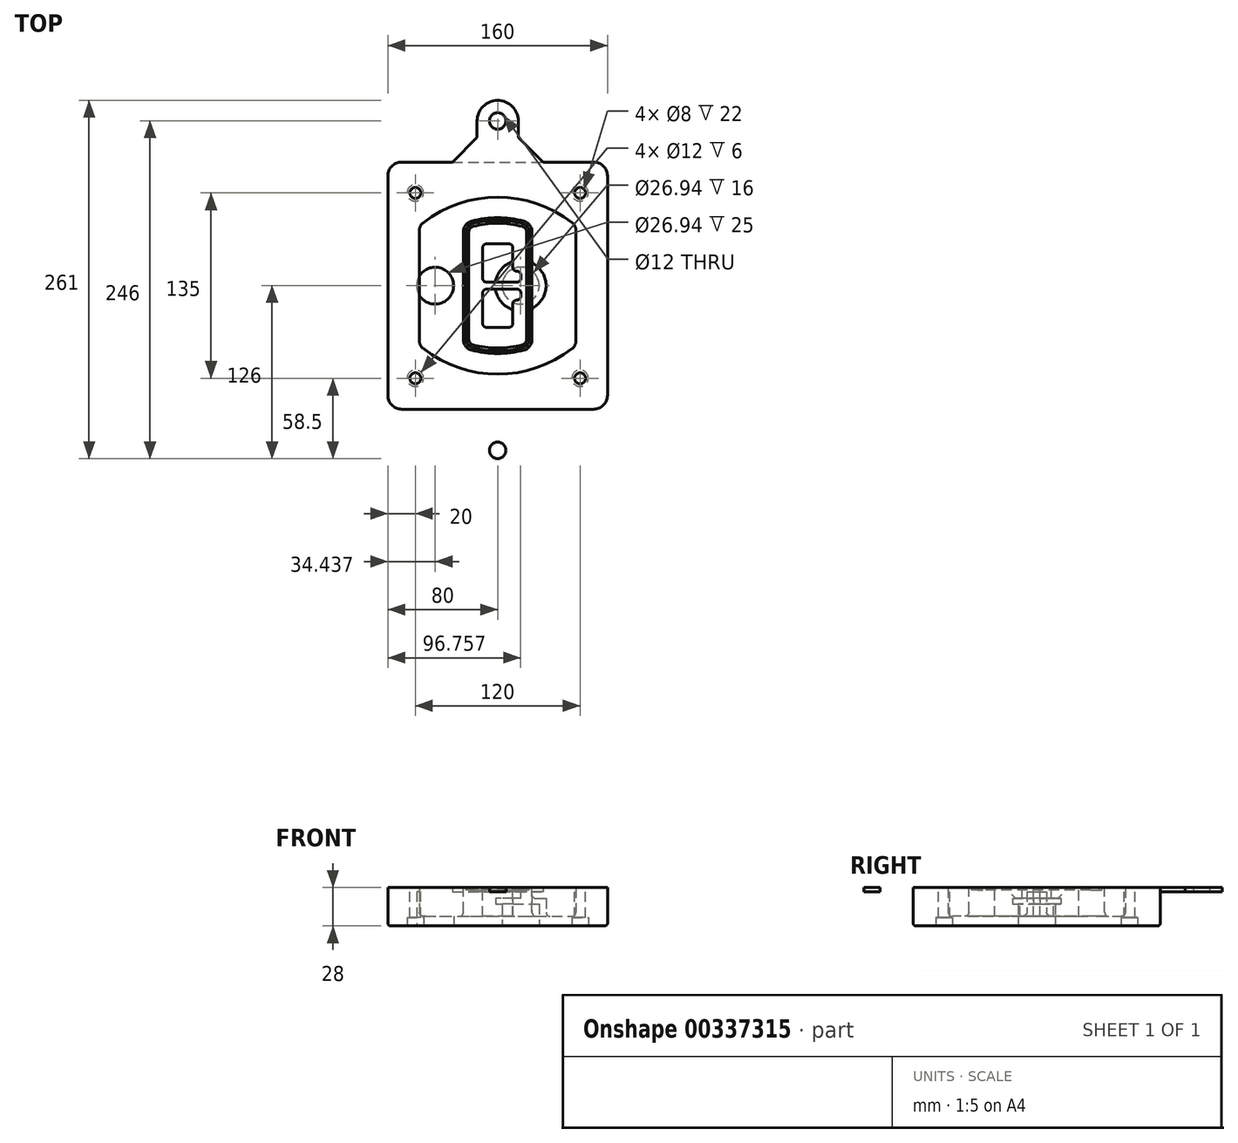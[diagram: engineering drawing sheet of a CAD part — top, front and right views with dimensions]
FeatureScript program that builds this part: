
annotation { "Feature Type Name" : "Feature", "Feature Type Description" : "" }
export const myFeature = defineFeature(function(context is Context, id is Id, definition is map)
    precondition{}
    {
        {
            var Q0;
            Q0=qCreatedBy(makeId("Top.planeOp"),FACE);
            var sketch = newSketch(context, id + "F0", { "sketchPlane" : qUnion([Q0])});
            skPoint(sketch, "E0.rect.middle", {"position": v(0, 0) * mm});
            skLineSegment(sketch, "E1.bottom", {"start": v(-70, -90) * mm, "end": v(70, -90) * mm});
            skLineSegment(sketch, "E1.top", {"start": v(-70, 90) * mm, "end": v(70, 90) * mm});
            skLineSegment(sketch, "E1.left", {"start": v(-80, -80) * mm, "end": v(-80, 80) * mm});
            skLineSegment(sketch, "E1.right", {"start": v(80, -80) * mm, "end": v(80, 80) * mm});
            skLineSegment(sketch, "E2", {"start": v(-80, 90) * mm, "end": v(80, -90) * mm, "construction": true});
            skLineSegment(sketch, "E3", {"start": v(80, 90) * mm, "end": v(-80, -90) * mm, "construction": true});
            skCircle(sketch, "E4", {"center": v(-60, 67.5) * mm, "radius": 4 * mm});
            skCircle(sketch, "E5", {"center": v(60, 67.5) * mm, "radius": 4 * mm});
            skCircle(sketch, "E6", {"center": v(60, -67.5) * mm, "radius": 4 * mm});
            skCircle(sketch, "E7", {"center": v(-60, -67.5) * mm, "radius": 4 * mm});
            skLineSegment(sketch, "E8", {"start": v(-60, 67.5) * mm, "end": v(60, 67.5) * mm, "construction": true});
            skLineSegment(sketch, "E9", {"start": v(60, 67.5) * mm, "end": v(60, -67.5) * mm, "construction": true});
            skLineSegment(sketch, "E10", {"start": v(60, -67.5) * mm, "end": v(-60, -67.5) * mm, "construction": true});
            skLineSegment(sketch, "E11", {"start": v(-60, -67.5) * mm, "end": v(-60, 67.5) * mm, "construction": true});
            skLineSegment(sketch, "E12", {"start": v(-60, 40.3) * mm, "end": v(-60, -40.3) * mm});
            skLineSegment(sketch, "E13", {"start": v(60, 40.3) * mm, "end": v(60, -40.3) * mm});
            skArc(sketch, "E14", {"start": v(56.15, 48.18) * mm, "mid": v(0, 67.5) * mm, "end": v(-56.15, 48.18) * mm});
            skArc(sketch, "E15", {"start": v(-56.15, -48.18) * mm, "mid": v(0, -67.5) * mm, "end": v(56.15, -48.18) * mm});
            skLineSegment(sketch, "E16", {"start": v(-60, 0) * mm, "end": v(60, 0) * mm, "construction": true});
            skPoint(sketch, "E17.visualSharp", {"position": v(-60, -45) * mm});
            skArc(sketch, "E17.filletArc", {"start": v(-60, -40.3) * mm, "mid": v(-58.99, -44.68) * mm, "end": v(-56.15, -48.18) * mm});
            skPoint(sketch, "E18.visualSharp", {"position": v(-60, 45) * mm});
            skArc(sketch, "E18.filletArc", {"start": v(-56.15, 48.18) * mm, "mid": v(-58.99, 44.68) * mm, "end": v(-60, 40.3) * mm});
            skPoint(sketch, "E19.visualSharp", {"position": v(60, 45) * mm});
            skArc(sketch, "E19.filletArc", {"start": v(60, 40.3) * mm, "mid": v(58.99, 44.68) * mm, "end": v(56.15, 48.18) * mm});
            skPoint(sketch, "E20.visualSharp", {"position": v(60, -45) * mm});
            skArc(sketch, "E20.filletArc", {"start": v(56.15, -48.18) * mm, "mid": v(58.99, -44.68) * mm, "end": v(60, -40.3) * mm});
            skPoint(sketch, "E21.visualSharp", {"position": v(-80, 90) * mm});
            skArc(sketch, "E21.filletArc", {"start": v(-70, 90) * mm, "mid": v(-77.07, 87.07) * mm, "end": v(-80, 80) * mm});
            skPoint(sketch, "E22.visualSharp", {"position": v(80, 90) * mm});
            skArc(sketch, "E22.filletArc", {"start": v(80, 80) * mm, "mid": v(77.07, 87.07) * mm, "end": v(70, 90) * mm});
            skPoint(sketch, "E23.visualSharp", {"position": v(80, -90) * mm});
            skArc(sketch, "E23.filletArc", {"start": v(70, -90) * mm, "mid": v(77.07, -87.07) * mm, "end": v(80, -80) * mm});
            skPoint(sketch, "E24.visualSharp", {"position": v(-80, -90) * mm});
            skArc(sketch, "E24.filletArc", {"start": v(-80, -80) * mm, "mid": v(-77.07, -87.07) * mm, "end": v(-70, -90) * mm});
            skArc(sketch, "E25.0", {"start": v(57, 40.3) * mm, "mid": v(56.3, 43.36) * mm, "end": v(54.3, 45.81) * mm});
            skLineSegment(sketch, "E25.1", {"start": v(57, 40.3) * mm, "end": v(57, -40.3) * mm});
            skArc(sketch, "E25.2", {"start": v(54.3, -45.81) * mm, "mid": v(56.3, -43.36) * mm, "end": v(57, -40.3) * mm});
            skArc(sketch, "E25.3", {"start": v(-54.3, -45.81) * mm, "mid": v(0, -64.5) * mm, "end": v(54.3, -45.81) * mm});
            skArc(sketch, "E25.4", {"start": v(-57, -40.3) * mm, "mid": v(-56.3, -43.36) * mm, "end": v(-54.3, -45.81) * mm});
            skArc(sketch, "E25.5", {"start": v(54.3, 45.81) * mm, "mid": v(0, 64.5) * mm, "end": v(-54.3, 45.81) * mm});
            skLineSegment(sketch, "E25.6", {"start": v(-57, 40.3) * mm, "end": v(-57, -40.3) * mm});
            skArc(sketch, "E25.7", {"start": v(-54.3, 45.81) * mm, "mid": v(-56.3, 43.36) * mm, "end": v(-57, 40.3) * mm});
            skArc(sketch, "E26.0", {"start": v(-58.62, 51.33) * mm, "mid": v(-62.58, 46.43) * mm, "end": v(-64, 40.3) * mm});
            skArc(sketch, "E26.1", {"start": v(58.62, 51.33) * mm, "mid": v(0, 71.5) * mm, "end": v(-58.62, 51.33) * mm});
            skArc(sketch, "E26.2", {"start": v(64, 40.3) * mm, "mid": v(62.58, 46.43) * mm, "end": v(58.62, 51.33) * mm});
            skLineSegment(sketch, "E26.3", {"start": v(64, 40.3) * mm, "end": v(64, -40.3) * mm});
            skArc(sketch, "E26.4", {"start": v(58.62, -51.33) * mm, "mid": v(62.58, -46.43) * mm, "end": v(64, -40.3) * mm});
            skLineSegment(sketch, "E26.5", {"start": v(-64, 40.3) * mm, "end": v(-64, -40.3) * mm});
            skArc(sketch, "E26.6", {"start": v(-58.62, -51.33) * mm, "mid": v(0, -71.5) * mm, "end": v(58.62, -51.33) * mm});
            skArc(sketch, "E26.7", {"start": v(-64, -40.3) * mm, "mid": v(-62.58, -46.43) * mm, "end": v(-58.62, -51.33) * mm});
            skSolve(sketch);
        }
        {
            var Q0;
            Q0=makeQuery(id+"F0.imprint","IMPRINT",FACE,{"disambiguationData":[TD([[makeQuery(id+"F0.imprint","IMPRINT",EDGE,{"derivedFrom":sQuery(id+"F0.wireOp",EDGE,"E1.bottom")}),1.0]])]});
            var Q1;
            Q1=makeQuery(id+"F0.imprint","IMPRINT",FACE,{"disambiguationData":[TD([[makeQuery(id+"F0.imprint","IMPRINT",EDGE,{"derivedFrom":sQuery(id+"F0.wireOp",EDGE,"E12")}),1.0]])]});
            var Q2;
            Q2=makeQuery(id+"F0.imprint","IMPRINT",FACE,{"disambiguationData":[TD([[makeQuery(id+"F0.imprint","IMPRINT",EDGE,{"derivedFrom":sQuery(id+"F0.wireOp",EDGE,"E25.0")}),1.0]])]});
            var Q3;
            Q3=makeQuery(id+"F0.imprint","IMPRINT",FACE,{"disambiguationData":[TD([[makeQuery(id+"F0.imprint","IMPRINT",EDGE,{"derivedFrom":sQuery(id+"F0.wireOp",EDGE,"E12")}),-1.0]])]});
            extrude(context, id + "F1", {"entities" : qUnion([Q0, Q1, Q2, Q3]), "oppositeDirection" : true, "depth" : 25 * mm});
        }
        {
            var Q0;
            Q0=makeQuery(id+"F0.imprint","IMPRINT",FACE,{"disambiguationData":[TD([[makeQuery(id+"F0.imprint","IMPRINT",EDGE,{"derivedFrom":sQuery(id+"F0.wireOp",EDGE,"E12")}),1.0]])]});
            extrude(context, id + "F2", {"entities" : qUnion([Q0]), "operationType" : NewBodyOperationType.ADD, "depth" : 3 * mm});
        }
        {
            var Q0;
            Q0=makeQuery(id+"F0.imprint","IMPRINT",FACE,{"disambiguationData":[TD([[makeQuery(id+"F0.imprint","IMPRINT",EDGE,{"derivedFrom":sQuery(id+"F0.wireOp",EDGE,"E25.0")}),1.0]])]});
            extrude(context, id + "F3", {"entities" : qUnion([Q0]), "operationType" : NewBodyOperationType.REMOVE, "oppositeDirection" : true, "depth" : 18 * mm});
        }
        {
            var Q0;
            Q0=makeQuery(id+"F2.opExtrude","CAP_FACE",FACE,{"disambiguationData":[OSD([sQuery(id+"F0.wireOp",EDGE,"E12"),sQuery(id+"F0.wireOp",EDGE,"E13"),sQuery(id+"F0.wireOp",EDGE,"E14"),sQuery(id+"F0.wireOp",EDGE,"E15"),sQuery(id+"F0.wireOp",EDGE,"E17.filletArc"),sQuery(id+"F0.wireOp",EDGE,"E18.filletArc"),sQuery(id+"F0.wireOp",EDGE,"E19.filletArc"),sQuery(id+"F0.wireOp",EDGE,"E20.filletArc"),sQuery(id+"F0.wireOp",EDGE,"E25.0"),sQuery(id+"F0.wireOp",EDGE,"E25.1"),sQuery(id+"F0.wireOp",EDGE,"E25.2"),sQuery(id+"F0.wireOp",EDGE,"E25.3"),sQuery(id+"F0.wireOp",EDGE,"E25.4"),sQuery(id+"F0.wireOp",EDGE,"E25.5"),sQuery(id+"F0.wireOp",EDGE,"E25.6"),sQuery(id+"F0.wireOp",EDGE,"E25.7")])],"isStart":false});
            var sketch = newSketch(context, id + "F4", { "sketchPlane" : qUnion([Q0])});
            skArc(sketch, "E27.0", {"start": v(-19.08, -46.97) * mm, "mid": v(0, -49.5) * mm, "end": v(19.08, -46.97) * mm});
            skArc(sketch, "E28.0", {"start": v(19.08, 46.97) * mm, "mid": v(0, 49.5) * mm, "end": v(-19.08, 46.97) * mm});
            skLineSegment(sketch, "E29", {"start": v(-25, 39.25) * mm, "end": v(-25, -39.25) * mm});
            skLineSegment(sketch, "E30", {"start": v(25, 39.25) * mm, "end": v(25, -39.25) * mm});
            skLineSegment(sketch, "E31", {"start": v(-25, 45.1) * mm, "end": v(25, 45.1) * mm, "construction": true});
            skLineSegment(sketch, "E32", {"start": v(-25, -45.1) * mm, "end": v(25, -45.1) * mm, "construction": true});
            skPoint(sketch, "E33.visualSharp", {"position": v(-25, 45.1) * mm});
            skArc(sketch, "E33.filletArc", {"start": v(-19.08, 46.97) * mm, "mid": v(-23.35, 44.11) * mm, "end": v(-25, 39.25) * mm});
            skPoint(sketch, "E34.visualSharp", {"position": v(25, 45.1) * mm});
            skArc(sketch, "E34.filletArc", {"start": v(25, 39.25) * mm, "mid": v(23.35, 44.11) * mm, "end": v(19.08, 46.97) * mm});
            skPoint(sketch, "E35.visualSharp", {"position": v(25, -45.1) * mm});
            skArc(sketch, "E35.filletArc", {"start": v(19.08, -46.97) * mm, "mid": v(23.35, -44.11) * mm, "end": v(25, -39.25) * mm});
            skPoint(sketch, "E36.visualSharp", {"position": v(-25, -45.1) * mm});
            skArc(sketch, "E36.filletArc", {"start": v(-25, -39.25) * mm, "mid": v(-23.35, -44.11) * mm, "end": v(-19.08, -46.97) * mm});
            skArc(sketch, "E37.0", {"start": v(54.3, 45.81) * mm, "mid": v(0, 64.5) * mm, "end": v(-54.3, 45.81) * mm});
            skArc(sketch, "E37.1", {"start": v(-54.3, 45.81) * mm, "mid": v(-56.3, 43.36) * mm, "end": v(-57, 40.3) * mm});
            skLineSegment(sketch, "E37.2", {"start": v(-57, 40.3) * mm, "end": v(-57, -40.3) * mm});
            skArc(sketch, "E37.3", {"start": v(-57, -40.3) * mm, "mid": v(-56.3, -43.36) * mm, "end": v(-54.3, -45.81) * mm});
            skArc(sketch, "E37.4", {"start": v(-54.3, -45.81) * mm, "mid": v(0, -64.5) * mm, "end": v(54.3, -45.81) * mm});
            skArc(sketch, "E37.5", {"start": v(54.3, -45.81) * mm, "mid": v(56.3, -43.36) * mm, "end": v(57, -40.3) * mm});
            skLineSegment(sketch, "E37.6", {"start": v(57, 40.3) * mm, "end": v(57, -40.3) * mm});
            skArc(sketch, "E37.7", {"start": v(57, 40.3) * mm, "mid": v(56.3, 43.36) * mm, "end": v(54.3, 45.81) * mm});
            skLineSegment(sketch, "E38.0", {"start": v(23, 39.25) * mm, "end": v(23, -39.25) * mm});
            skArc(sketch, "E38.1", {"start": v(18.56, -45.04) * mm, "mid": v(21.76, -42.9) * mm, "end": v(23, -39.25) * mm});
            skArc(sketch, "E38.2", {"start": v(-18.56, -45.04) * mm, "mid": v(0, -47.5) * mm, "end": v(18.56, -45.04) * mm});
            skArc(sketch, "E38.3", {"start": v(-23, -39.25) * mm, "mid": v(-21.76, -42.9) * mm, "end": v(-18.56, -45.04) * mm});
            skLineSegment(sketch, "E38.4", {"start": v(-23, 39.25) * mm, "end": v(-23, -39.25) * mm});
            skArc(sketch, "E38.5", {"start": v(23, 39.25) * mm, "mid": v(21.76, 42.9) * mm, "end": v(18.56, 45.04) * mm});
            skArc(sketch, "E38.6", {"start": v(-18.56, 45.04) * mm, "mid": v(-21.76, 42.9) * mm, "end": v(-23, 39.25) * mm});
            skArc(sketch, "E38.7", {"start": v(18.56, 45.04) * mm, "mid": v(0, 47.5) * mm, "end": v(-18.56, 45.04) * mm});
            skArc(sketch, "E39.0", {"start": v(21, 39.25) * mm, "mid": v(20.18, 41.68) * mm, "end": v(18.04, 43.1) * mm});
            skLineSegment(sketch, "E39.1", {"start": v(21, 39.25) * mm, "end": v(21, -39.25) * mm});
            skArc(sketch, "E39.2", {"start": v(18.04, -43.1) * mm, "mid": v(20.18, -41.68) * mm, "end": v(21, -39.25) * mm});
            skArc(sketch, "E39.3", {"start": v(-18.04, -43.1) * mm, "mid": v(0, -45.5) * mm, "end": v(18.04, -43.1) * mm});
            skArc(sketch, "E39.4", {"start": v(-21, -39.25) * mm, "mid": v(-20.18, -41.68) * mm, "end": v(-18.04, -43.1) * mm});
            skArc(sketch, "E39.5", {"start": v(18.04, 43.1) * mm, "mid": v(0, 45.5) * mm, "end": v(-18.04, 43.1) * mm});
            skLineSegment(sketch, "E39.6", {"start": v(-21, 39.25) * mm, "end": v(-21, -39.25) * mm});
            skArc(sketch, "E39.7", {"start": v(-18.04, 43.1) * mm, "mid": v(-20.18, 41.68) * mm, "end": v(-21, 39.25) * mm});
            skLineSegment(sketch, "E40", {"start": v(-25, 0) * mm, "end": v(25, 0) * mm, "construction": true});
            skLineSegment(sketch, "E41", {"start": v(-11, 5.5) * mm, "end": v(-11, 27.5) * mm});
            skLineSegment(sketch, "E42", {"start": v(-8, 30.5) * mm, "end": v(8, 30.5) * mm});
            skLineSegment(sketch, "E43", {"start": v(11, 27.5) * mm, "end": v(11, 13.5) * mm});
            skLineSegment(sketch, "E44", {"start": v(14, 10.5) * mm, "end": v(14, 10.5) * mm});
            skLineSegment(sketch, "E45", {"start": v(17, 7.5) * mm, "end": v(17, 5.5) * mm});
            skLineSegment(sketch, "E46", {"start": v(14, 2.5) * mm, "end": v(-8, 2.5) * mm});
            skPoint(sketch, "E47.visualSharp", {"position": v(-11, 30.5) * mm});
            skArc(sketch, "E47.filletArc", {"start": v(-8, 30.5) * mm, "mid": v(-10.12, 29.62) * mm, "end": v(-11, 27.5) * mm});
            skPoint(sketch, "E48.visualSharp", {"position": v(11, 30.5) * mm});
            skArc(sketch, "E48.filletArc", {"start": v(11, 27.5) * mm, "mid": v(10.12, 29.62) * mm, "end": v(8, 30.5) * mm});
            skPoint(sketch, "E49.visualSharp", {"position": v(11, 10.5) * mm});
            skArc(sketch, "E49.filletArc", {"start": v(11, 13.5) * mm, "mid": v(11.88, 11.38) * mm, "end": v(14, 10.5) * mm});
            skPoint(sketch, "E50.visualSharp", {"position": v(17, 10.5) * mm});
            skArc(sketch, "E50.filletArc", {"start": v(17, 7.5) * mm, "mid": v(16.12, 9.62) * mm, "end": v(14, 10.5) * mm});
            skPoint(sketch, "E51.visualSharp", {"position": v(17, 2.5) * mm});
            skArc(sketch, "E51.filletArc", {"start": v(14, 2.5) * mm, "mid": v(16.12, 3.38) * mm, "end": v(17, 5.5) * mm});
            skPoint(sketch, "E52.visualSharp", {"position": v(-11, 2.5) * mm});
            skArc(sketch, "E52.filletArc", {"start": v(-11, 5.5) * mm, "mid": v(-10.12, 3.38) * mm, "end": v(-8, 2.5) * mm});
            skLineSegment(sketch, "E53.0.MirrorCS", {"start": v(14, -2.5) * mm, "end": v(-8, -2.5) * mm});
            skArc(sketch, "E54.0.MirrorCS", {"start": v(-11, -5.5) * mm, "mid": v(-10.12, -3.38) * mm, "end": v(-8, -2.5) * mm});
            skLineSegment(sketch, "E55.0.MirrorCS", {"start": v(-11, -5.5) * mm, "end": v(-11, -27.5) * mm});
            skArc(sketch, "E56.0.MirrorCS", {"start": v(-8, -30.5) * mm, "mid": v(-10.12, -29.62) * mm, "end": v(-11, -27.5) * mm});
            skLineSegment(sketch, "E57.0.MirrorCS", {"start": v(-8, -30.5) * mm, "end": v(8, -30.5) * mm});
            skArc(sketch, "E58.0.MirrorCS", {"start": v(11, -27.5) * mm, "mid": v(10.12, -29.62) * mm, "end": v(8, -30.5) * mm});
            skLineSegment(sketch, "E59.0.MirrorCS", {"start": v(11, -27.5) * mm, "end": v(11, -13.5) * mm});
            skArc(sketch, "E60.0.MirrorCS", {"start": v(11, -13.5) * mm, "mid": v(11.88, -11.38) * mm, "end": v(14, -10.5) * mm});
            skArc(sketch, "E61.0.MirrorCS", {"start": v(17, -7.5) * mm, "mid": v(16.12, -9.62) * mm, "end": v(14, -10.5) * mm});
            skLineSegment(sketch, "E62.0.MirrorCS", {"start": v(17, -7.5) * mm, "end": v(17, -5.5) * mm});
            skArc(sketch, "E63.0.MirrorCS", {"start": v(14, -2.5) * mm, "mid": v(16.12, -3.38) * mm, "end": v(17, -5.5) * mm});
            skSolve(sketch);
        }
        {
            var Q0;
            Q0=makeQuery(id+"F4.imprint","IMPRINT",FACE,{"disambiguationData":[TD([[makeQuery(id+"F4.imprint","IMPRINT",EDGE,{"derivedFrom":sQuery(id+"F4.wireOp",EDGE,"E27.0")}),1.0]])]});
            var Q1;
            Q1=makeQuery(id+"F4.imprint","IMPRINT",FACE,{"disambiguationData":[TD([[makeQuery(id+"F4.imprint","IMPRINT",EDGE,{"derivedFrom":sQuery(id+"F4.wireOp",EDGE,"E38.0")}),-1.0]])]});
            var Q2;
            Q2=makeQuery(id+"F4.imprint","IMPRINT",FACE,{"disambiguationData":[TD([[makeQuery(id+"F4.imprint","IMPRINT",EDGE,{"derivedFrom":sQuery(id+"F4.wireOp",EDGE,"E39.0")}),1.0]])]});
            extrude(context, id + "F5", {"entities" : qUnion([Q0, Q1, Q2]), "operationType" : NewBodyOperationType.ADD, "endBound" : BoundingType.UP_TO_NEXT, "oppositeDirection" : true, "depth" : 25 * mm});
        }
        {
            var Q0;
            Q0=makeQuery(id+"F4.imprint","IMPRINT",FACE,{"disambiguationData":[TD([[makeQuery(id+"F4.imprint","IMPRINT",EDGE,{"derivedFrom":sQuery(id+"F4.wireOp",EDGE,"E38.0")}),-1.0]])]});
            extrude(context, id + "F6", {"entities" : qUnion([Q0]), "operationType" : NewBodyOperationType.REMOVE, "oppositeDirection" : true, "depth" : 2 * mm});
        }
        {
            var Q0;
            Q0=makeQuery(id+"F1.opExtrude","CAP_FACE",FACE,{"disambiguationData":[OSD([sQuery(id+"F0.wireOp",EDGE,"E1.bottom"),sQuery(id+"F0.wireOp",EDGE,"E1.top"),sQuery(id+"F0.wireOp",EDGE,"E1.left"),sQuery(id+"F0.wireOp",EDGE,"E1.right"),sQuery(id+"F0.wireOp",EDGE,"E4"),sQuery(id+"F0.wireOp",EDGE,"E5"),sQuery(id+"F0.wireOp",EDGE,"E6"),sQuery(id+"F0.wireOp",EDGE,"E7"),sQuery(id+"F0.wireOp",EDGE,"E21.filletArc"),sQuery(id+"F0.wireOp",EDGE,"E22.filletArc"),sQuery(id+"F0.wireOp",EDGE,"E23.filletArc"),sQuery(id+"F0.wireOp",EDGE,"E24.filletArc")])],"isStart":false});
            var sketch = newSketch(context, id + "F7", { "sketchPlane" : qUnion([Q0])});
            skCircle(sketch, "E64", {"center": v(16.76, 0) * mm, "radius": 13.47 * mm});
            skCircle(sketch, "E65", {"center": v(-45.56, 0) * mm, "radius": 13.47 * mm});
            skLineSegment(sketch, "E66", {"start": v(80, 0) * mm, "end": v(-80, 0) * mm});
            skCircle(sketch, "E67", {"center": v(16.76, 0) * mm, "radius": 18.47 * mm});
            skCircle(sketch, "E68", {"center": v(60, -67.5) * mm, "radius": 6 * mm});
            skCircle(sketch, "E69", {"center": v(-60, -67.5) * mm, "radius": 6 * mm});
            skCircle(sketch, "E70", {"center": v(-60, 67.5) * mm, "radius": 6 * mm});
            skCircle(sketch, "E71", {"center": v(60, 67.5) * mm, "radius": 6 * mm});
            skSolve(sketch);
        }
        {
            var Q0;
            {var subQ1=sQuery(id+"F7.wireOp",EDGE,"E66");var subQ4=sQuery(id+"F7.wireOp",EDGE,"E64");var subQ6=makeQuery(id+"F7.imprint","INTERSECT",VERTEX,{"disambiguationData":[OD(0.0)],"derivedFrom":[subQ4,subQ1]});Q0=makeQuery(id+"F7.imprint","IMPRINT",FACE,{"disambiguationData":[TD([[makeQuery(id+"F7.imprint","IMPRINT",EDGE,{"disambiguationData":[TD([[subQ6,-1.0]])],"derivedFrom":subQ4}),-1.0]])]});}
            var Q1;
            {var subQ0=sQuery(id+"F7.wireOp",EDGE,"E66");var subQ1=sQuery(id+"F7.wireOp",EDGE,"E64");var subQ3=makeQuery(id+"F7.imprint","INTERSECT",VERTEX,{"disambiguationData":[OD(0.0)],"derivedFrom":[subQ1,subQ0]});Q1=makeQuery(id+"F7.imprint","IMPRINT",FACE,{"disambiguationData":[TD([[makeQuery(id+"F7.imprint","IMPRINT",EDGE,{"disambiguationData":[TD([[subQ3,-1.0]])],"derivedFrom":subQ1}),1.0]])]});}
            var Q2;
            {var subQ0=sQuery(id+"F7.wireOp",EDGE,"E66");var subQ1=sQuery(id+"F7.wireOp",EDGE,"E64");var subQ3=makeQuery(id+"F7.imprint","INTERSECT",VERTEX,{"disambiguationData":[OD(0.0)],"derivedFrom":[subQ1,subQ0]});Q2=makeQuery(id+"F7.imprint","IMPRINT",FACE,{"disambiguationData":[TD([[makeQuery(id+"F7.imprint","IMPRINT",EDGE,{"disambiguationData":[TD([[subQ3,1.0]])],"derivedFrom":subQ1}),1.0]])]});}
            var Q3;
            {var subQ1=sQuery(id+"F7.wireOp",EDGE,"E66");var subQ4=sQuery(id+"F7.wireOp",EDGE,"E64");var subQ6=makeQuery(id+"F7.imprint","INTERSECT",VERTEX,{"disambiguationData":[OD(0.0)],"derivedFrom":[subQ4,subQ1]});Q3=makeQuery(id+"F7.imprint","IMPRINT",FACE,{"disambiguationData":[TD([[makeQuery(id+"F7.imprint","IMPRINT",EDGE,{"disambiguationData":[TD([[subQ6,1.0]])],"derivedFrom":subQ4}),-1.0]])]});}
            extrude(context, id + "F8", {"entities" : qUnion([Q0, Q1, Q2, Q3]), "operationType" : NewBodyOperationType.ADD, "oppositeDirection" : true, "depth" : 20 * mm});
        }
        {
            var Q0;
            {var subQ0=sQuery(id+"F7.wireOp",EDGE,"E66");var subQ1=sQuery(id+"F7.wireOp",EDGE,"E64");var subQ3=makeQuery(id+"F7.imprint","INTERSECT",VERTEX,{"disambiguationData":[OD(0.0)],"derivedFrom":[subQ1,subQ0]});Q0=makeQuery(id+"F7.imprint","IMPRINT",FACE,{"disambiguationData":[TD([[makeQuery(id+"F7.imprint","IMPRINT",EDGE,{"disambiguationData":[TD([[subQ3,-1.0]])],"derivedFrom":subQ1}),1.0]])]});}
            var Q1;
            {var subQ0=sQuery(id+"F7.wireOp",EDGE,"E66");var subQ1=sQuery(id+"F7.wireOp",EDGE,"E64");var subQ3=makeQuery(id+"F7.imprint","INTERSECT",VERTEX,{"disambiguationData":[OD(0.0)],"derivedFrom":[subQ1,subQ0]});Q1=makeQuery(id+"F7.imprint","IMPRINT",FACE,{"disambiguationData":[TD([[makeQuery(id+"F7.imprint","IMPRINT",EDGE,{"disambiguationData":[TD([[subQ3,1.0]])],"derivedFrom":subQ1}),1.0]])]});}
            extrude(context, id + "F9", {"entities" : qUnion([Q0, Q1]), "operationType" : NewBodyOperationType.REMOVE, "oppositeDirection" : true, "depth" : 16 * mm});
        }
        {
            var Q0;
            {var subQ0=sQuery(id+"F7.wireOp",EDGE,"E66");var subQ1=sQuery(id+"F7.wireOp",EDGE,"E65");var subQ3=makeQuery(id+"F7.imprint","INTERSECT",VERTEX,{"disambiguationData":[OD(0.0)],"derivedFrom":[subQ1,subQ0]});Q0=makeQuery(id+"F7.imprint","IMPRINT",FACE,{"disambiguationData":[TD([[makeQuery(id+"F7.imprint","IMPRINT",EDGE,{"disambiguationData":[TD([[subQ3,-1.0]])],"derivedFrom":subQ1}),1.0]])]});}
            var Q1;
            {var subQ0=sQuery(id+"F7.wireOp",EDGE,"E66");var subQ1=sQuery(id+"F7.wireOp",EDGE,"E65");var subQ3=makeQuery(id+"F7.imprint","INTERSECT",VERTEX,{"disambiguationData":[OD(0.0)],"derivedFrom":[subQ1,subQ0]});Q1=makeQuery(id+"F7.imprint","IMPRINT",FACE,{"disambiguationData":[TD([[makeQuery(id+"F7.imprint","IMPRINT",EDGE,{"disambiguationData":[TD([[subQ3,1.0]])],"derivedFrom":subQ1}),1.0]])]});}
            extrude(context, id + "F10", {"entities" : qUnion([Q0, Q1]), "operationType" : NewBodyOperationType.REMOVE, "oppositeDirection" : true, "depth" : 25 * mm});
        }
        {
            var Q0;
            Q0=makeQuery(id+"F7.imprint","IMPRINT",FACE,{"disambiguationData":[TD([[makeQuery(id+"F7.imprint","IMPRINT",EDGE,{"derivedFrom":sQuery(id+"F7.wireOp",EDGE,"E68")}),1.0]])]});
            var Q1;
            Q1=makeQuery(id+"F7.imprint","IMPRINT",FACE,{"disambiguationData":[TD([[makeQuery(id+"F7.imprint","IMPRINT",EDGE,{"derivedFrom":makeQuery(id+"F1.opExtrude","CAP_EDGE",EDGE,{"disambiguationData":[OSD([sQuery(id+"F0.wireOp",EDGE,"E5")])],"isStart":false})}),-1.0]])]});
            var Q2;
            Q2=makeQuery(id+"F7.imprint","IMPRINT",FACE,{"disambiguationData":[TD([[makeQuery(id+"F7.imprint","IMPRINT",EDGE,{"derivedFrom":sQuery(id+"F7.wireOp",EDGE,"E69")}),1.0]])]});
            var Q3;
            Q3=makeQuery(id+"F7.imprint","IMPRINT",FACE,{"disambiguationData":[TD([[makeQuery(id+"F7.imprint","IMPRINT",EDGE,{"derivedFrom":makeQuery(id+"F1.opExtrude","CAP_EDGE",EDGE,{"disambiguationData":[OSD([sQuery(id+"F0.wireOp",EDGE,"E4")])],"isStart":false})}),-1.0]])]});
            var Q4;
            Q4=makeQuery(id+"F7.imprint","IMPRINT",FACE,{"disambiguationData":[TD([[makeQuery(id+"F7.imprint","IMPRINT",EDGE,{"derivedFrom":sQuery(id+"F7.wireOp",EDGE,"E70")}),1.0]])]});
            var Q5;
            Q5=makeQuery(id+"F7.imprint","IMPRINT",FACE,{"disambiguationData":[TD([[makeQuery(id+"F7.imprint","IMPRINT",EDGE,{"derivedFrom":makeQuery(id+"F1.opExtrude","CAP_EDGE",EDGE,{"disambiguationData":[OSD([sQuery(id+"F0.wireOp",EDGE,"E7")])],"isStart":false})}),-1.0]])]});
            var Q6;
            Q6=makeQuery(id+"F7.imprint","IMPRINT",FACE,{"disambiguationData":[TD([[makeQuery(id+"F7.imprint","IMPRINT",EDGE,{"derivedFrom":sQuery(id+"F7.wireOp",EDGE,"E71")}),1.0]])]});
            var Q7;
            Q7=makeQuery(id+"F7.imprint","IMPRINT",FACE,{"disambiguationData":[TD([[makeQuery(id+"F7.imprint","IMPRINT",EDGE,{"derivedFrom":makeQuery(id+"F1.opExtrude","CAP_EDGE",EDGE,{"disambiguationData":[OSD([sQuery(id+"F0.wireOp",EDGE,"E6")])],"isStart":false})}),-1.0]])]});
            extrude(context, id + "F11", {"entities" : qUnion([Q0, Q1, Q2, Q3, Q4, Q5, Q6, Q7]), "operationType" : NewBodyOperationType.REMOVE, "oppositeDirection" : true, "depth" : 6 * mm});
        }
        {
            var Q0;
            Q0=makeQuery(id+"F9.boolean.opBoolean","COPY",FACE,{"derivedFrom":makeQuery(id+"F9.opExtrude","CAP_FACE",FACE,{"disambiguationData":[OSD([sQuery(id+"F7.wireOp",EDGE,"E64")])],"isStart":false})});
            var sketch = newSketch(context, id + "F12", { "sketchPlane" : qUnion([Q0])});
            skArc(sketch, "E72.0", {"start": v(11, 17.55) * mm, "mid": v(2.57, 11.82) * mm, "end": v(-1.54, 2.5) * mm});
            skArc(sketch, "E72.1", {"start": v(-1.54, -2.5) * mm, "mid": v(2.57, -11.82) * mm, "end": v(11, -17.55) * mm});
            skLineSegment(sketch, "E73", {"start": v(-1.54, -2.5) * mm, "end": v(14, -2.5) * mm});
            skLineSegment(sketch, "E74.0", {"start": v(14, 2.5) * mm, "end": v(-1.54, 2.5) * mm});
            skArc(sketch, "E74.1", {"start": v(14, 2.5) * mm, "mid": v(16.12, 3.38) * mm, "end": v(17, 5.5) * mm});
            skLineSegment(sketch, "E74.2", {"start": v(17, 7.5) * mm, "end": v(17, 5.5) * mm});
            skArc(sketch, "E74.3", {"start": v(17, 7.5) * mm, "mid": v(16.12, 9.62) * mm, "end": v(14, 10.5) * mm});
            skArc(sketch, "E74.4", {"start": v(11, 13.5) * mm, "mid": v(11.88, 11.38) * mm, "end": v(14, 10.5) * mm});
            skLineSegment(sketch, "E74.5", {"start": v(11, 17.55) * mm, "end": v(11, 13.5) * mm});
            skLineSegment(sketch, "E74.7", {"start": v(14, -2.5) * mm, "end": v(-1.54, -2.5) * mm});
            skArc(sketch, "E74.8", {"start": v(14, -2.5) * mm, "mid": v(16.12, -3.38) * mm, "end": v(17, -5.5) * mm});
            skLineSegment(sketch, "E74.9", {"start": v(17, -7.5) * mm, "end": v(17, -5.5) * mm});
            skArc(sketch, "E74.10", {"start": v(17, -7.5) * mm, "mid": v(16.12, -9.62) * mm, "end": v(14, -10.5) * mm});
            skArc(sketch, "E74.11", {"start": v(11, -13.5) * mm, "mid": v(11.88, -11.38) * mm, "end": v(14, -10.5) * mm});
            skLineSegment(sketch, "E74.12", {"start": v(11, -17.55) * mm, "end": v(11, -13.5) * mm});
            skPoint(sketch, "E75.orphan", {"position": v(11, -27.5) * mm});
            skPoint(sketch, "E76.orphan", {"position": v(-8, -2.5) * mm});
            skPoint(sketch, "E77.orphan", {"position": v(-8, 2.5) * mm});
            skPoint(sketch, "E78.orphan", {"position": v(11, 27.5) * mm});
            skSolve(sketch);
        }
        {
            var Q0;
            {var subQ7=sQuery(id+"F12.wireOp",EDGE,"E72.0");var subQ14=sQuery(id+"F12.wireOp",EDGE,"E72.1");var subQ16=sQuery(id+"F12.wireOp",EDGE,"E74.1");var subQ18=sQuery(id+"F12.wireOp",EDGE,"E74.8");Q0=qUnion([makeQuery(id+"F12.imprint","IMPRINT",FACE,{"disambiguationData":[TD([[makeQuery(id+"F12.imprint","IMPRINT",EDGE,{"derivedFrom":subQ7}),1.0]])]}),makeQuery(id+"F12.imprint","IMPRINT",FACE,{"disambiguationData":[TD([[makeQuery(id+"F12.imprint","IMPRINT",EDGE,{"derivedFrom":subQ14}),1.0]])]}),makeQuery(id+"F12.imprint","IMPRINT",FACE,{"disambiguationData":[TD([[makeQuery(id+"F12.imprint","IMPRINT",EDGE,{"derivedFrom":subQ16}),1.0]])]}),makeQuery(id+"F12.imprint","IMPRINT",FACE,{"disambiguationData":[TD([[makeQuery(id+"F12.imprint","IMPRINT",EDGE,{"derivedFrom":subQ18}),-1.0]])]})]);}
            var Q1;
            Q1=makeQuery(id+"F5.boolean.opBoolean","SPLIT",FACE,{"disambiguationData":[TD([makeQuery(id+"F5.opExtrude","SWEPT_FACE",FACE,{"disambiguationData":[OSD([sQuery(id+"F4.wireOp",EDGE,"E41")])]})])],"derivedFrom":makeQuery(id+"F3.boolean.opBoolean","COPY",FACE,{"derivedFrom":makeQuery(id+"F3.opExtrude","CAP_FACE",FACE,{"disambiguationData":[OSD([sQuery(id+"F0.wireOp",EDGE,"E25.0"),sQuery(id+"F0.wireOp",EDGE,"E25.1"),sQuery(id+"F0.wireOp",EDGE,"E25.2"),sQuery(id+"F0.wireOp",EDGE,"E25.3"),sQuery(id+"F0.wireOp",EDGE,"E25.4"),sQuery(id+"F0.wireOp",EDGE,"E25.5"),sQuery(id+"F0.wireOp",EDGE,"E25.6"),sQuery(id+"F0.wireOp",EDGE,"E25.7")])],"isStart":false})})});
            extrude(context, id + "F13", {"entities" : qUnion([Q0]), "operationType" : NewBodyOperationType.REMOVE, "endBound" : BoundingType.UP_TO_SURFACE, "endBoundEntityFace" : qUnion([Q1]), "depth" : 25 * mm});
        }
        {
            var Q0;
            Q0=makeQuery(id+"F3.boolean.opBoolean","COPY",EDGE,{"derivedFrom":makeQuery(id+"F3.opExtrude","CAP_EDGE",EDGE,{"disambiguationData":[OSD([sQuery(id+"F0.wireOp",EDGE,"E25.6")])],"isStart":false})});
            var Q1;
            Q1=makeQuery(id+"F8.boolean.opBoolean","INTERSECT",EDGE,{"derivedFrom":[makeQuery(id+"F5.opExtrude","SWEPT_FACE",FACE,{"disambiguationData":[OSD([sQuery(id+"F4.wireOp",EDGE,"E30")])]}),makeQuery(id+"F8.opExtrude","CAP_FACE",FACE,{"disambiguationData":[OSD([sQuery(id+"F7.wireOp",EDGE,"E67")])],"isStart":false})]});
            var Q2;
            Q2=makeQuery(id+"F8.boolean.opBoolean","INTERSECT",EDGE,{"disambiguationData":[OD(1.0)],"derivedFrom":[makeQuery(id+"F5.opExtrude","SWEPT_FACE",FACE,{"disambiguationData":[OSD([sQuery(id+"F4.wireOp",EDGE,"E30")])]}),makeQuery(id+"F8.opExtrude","SWEPT_FACE",FACE,{"disambiguationData":[OSD([sQuery(id+"F7.wireOp",EDGE,"E67")])]})]});
            var Q3;
            {var subQ0=sQuery(id+"F4.wireOp",EDGE,"E30");Q3=makeQuery(id+"F8.boolean.opBoolean","SPLIT",EDGE,{"disambiguationData":[TD([makeQuery(id+"F5.opExtrude","SWEPT_FACE",FACE,{"disambiguationData":[OSD([sQuery(id+"F4.wireOp",EDGE,"E35.filletArc")])]})])],"derivedFrom":makeQuery(id+"F5.opExtrude","CAP_EDGE",EDGE,{"disambiguationData":[OSD([subQ0])],"isStart":false})});}
            var Q4;
            {var subQ0=sQuery(id+"F0.wireOp",EDGE,"E25.7");var subQ1=sQuery(id+"F0.wireOp",EDGE,"E25.1");var subQ2=sQuery(id+"F0.wireOp",EDGE,"E25.6");var subQ3=sQuery(id+"F0.wireOp",EDGE,"E25.5");var subQ4=sQuery(id+"F0.wireOp",EDGE,"E25.4");var subQ5=sQuery(id+"F0.wireOp",EDGE,"E25.0");var subQ6=sQuery(id+"F0.wireOp",EDGE,"E25.2");var subQ7=sQuery(id+"F0.wireOp",EDGE,"E25.3");Q4=makeQuery(id+"F8.boolean.opBoolean","INTERSECT",EDGE,{"derivedFrom":[makeQuery(id+"F5.boolean.opBoolean","SPLIT",FACE,{"disambiguationData":[TD([makeQuery(id+"F2.opExtrude","SWEPT_FACE",FACE,{"disambiguationData":[OSD([subQ5])]})])],"derivedFrom":makeQuery(id+"F3.boolean.opBoolean","COPY",FACE,{"derivedFrom":makeQuery(id+"F3.opExtrude","CAP_FACE",FACE,{"disambiguationData":[OSD([subQ5,subQ1,subQ6,subQ7,subQ4,subQ3,subQ2,subQ0])],"isStart":false})})}),makeQuery(id+"F8.opExtrude","SWEPT_FACE",FACE,{"disambiguationData":[OSD([sQuery(id+"F7.wireOp",EDGE,"E67")])]})]});}
            var Q5;
            Q5=makeQuery(id+"F8.boolean.opBoolean","INTERSECT",EDGE,{"disambiguationData":[OD(0.0)],"derivedFrom":[makeQuery(id+"F5.opExtrude","SWEPT_FACE",FACE,{"disambiguationData":[OSD([sQuery(id+"F4.wireOp",EDGE,"E30")])]}),makeQuery(id+"F8.opExtrude","SWEPT_FACE",FACE,{"disambiguationData":[OSD([sQuery(id+"F7.wireOp",EDGE,"E67")])]})]});
            fillet(context, id + "F14", {"entities" : qUnion([Q0, Q1, Q2, Q3, Q4, Q5]), "radius" : 3 * mm, "tangentPropagation" : true, "allowEdgeOverflow" : false});
        }
        {
            var Q0;
            Q0=makeQuery(id+"F1.opExtrude","CAP_EDGE",EDGE,{"disambiguationData":[OSD([sQuery(id+"F0.wireOp",EDGE,"E1.bottom")])],"isStart":false});
            fillet(context, id + "F15", {"entities" : qUnion([Q0]), "radius" : 2 * mm, "tangentPropagation" : true, "allowEdgeOverflow" : false});
        }
        {
            var Q0;
            {var subQ0=sQuery(id+"F0.wireOp",EDGE,"E21.filletArc");var subQ1=sQuery(id+"F0.wireOp",EDGE,"E7");var subQ2=sQuery(id+"F0.wireOp",EDGE,"E6");var subQ3=sQuery(id+"F0.wireOp",EDGE,"E5");var subQ4=sQuery(id+"F0.wireOp",EDGE,"E4");var subQ5=sQuery(id+"F0.wireOp",EDGE,"E22.filletArc");var subQ6=sQuery(id+"F0.wireOp",EDGE,"E1.bottom");var subQ7=sQuery(id+"F0.wireOp",EDGE,"E1.right");var subQ8=sQuery(id+"F0.wireOp",EDGE,"E1.top");var subQ9=sQuery(id+"F0.wireOp",EDGE,"E1.left");var subQ10=sQuery(id+"F0.wireOp",EDGE,"E23.filletArc");var subQ11=sQuery(id+"F0.wireOp",EDGE,"E24.filletArc");Q0=makeQuery(id+"F2.boolean.opBoolean","SPLIT",FACE,{"disambiguationData":[TD([makeQuery(id+"F1.opExtrude","SWEPT_FACE",FACE,{"disambiguationData":[OSD([subQ6])]})])],"derivedFrom":makeQuery(id+"F1.opExtrude","CAP_FACE",FACE,{"disambiguationData":[OSD([subQ6,subQ8,subQ9,subQ7,subQ4,subQ3,subQ2,subQ1,subQ0,subQ5,subQ10,subQ11])],"isStart":true})});}
            var sketch = newSketch(context, id + "F16", { "sketchPlane" : qUnion([Q0])});
            skPoint(sketch, "E79.centerSnap0", {"position": v(0, 90) * mm});
            skLineSegment(sketch, "E80", {"start": v(-33, 90) * mm, "end": v(-15, 108) * mm});
            skLineSegment(sketch, "E81", {"start": v(-15, 108) * mm, "end": v(-15, 120) * mm});
            skLineSegment(sketch, "E82", {"start": v(33, 90) * mm, "end": v(15, 108) * mm});
            skLineSegment(sketch, "E83", {"start": v(15, 108) * mm, "end": v(15, 120) * mm});
            skArc(sketch, "E84", {"start": v(15, 120) * mm, "mid": v(0, 135) * mm, "end": v(-15, 120) * mm});
            skCircle(sketch, "E85", {"center": v(0, 120) * mm, "radius": 6 * mm});
            skLineSegment(sketch, "E86", {"start": v(-80, 0) * mm, "end": v(80, 0) * mm, "construction": true});
            skLineSegment(sketch, "E87", {"start": v(0, 90) * mm, "end": v(0, 120) * mm, "construction": true});
            skLineSegment(sketch, "E88.MirrorCS", {"start": v(0, -90) * mm, "end": v(0, -120) * mm, "construction": true});
            skCircle(sketch, "E89.MirrorC", {"center": v(0, -120) * mm, "radius": 6 * mm});
            skArc(sketch, "E90.MirrorCS", {"start": v(15, -120) * mm, "mid": v(0, -135) * mm, "end": v(-15, -120) * mm});
            skLineSegment(sketch, "E91.MirrorCS", {"start": v(15, -108) * mm, "end": v(15, -120) * mm});
            skLineSegment(sketch, "E92.MirrorCS", {"start": v(33, -90) * mm, "end": v(15, -108) * mm});
            skLineSegment(sketch, "E93.MirrorCS", {"start": v(-15, -108) * mm, "end": v(-15, -120) * mm});
            skLineSegment(sketch, "E94.MirrorCS", {"start": v(-33, -90) * mm, "end": v(-15, -108) * mm});
            skPoint(sketch, "E95.MirrorP", {"position": v(0, -90) * mm});
            skSolve(sketch);
        }
        {
            var Q0;
            Q0=makeQuery(id+"F16.imprint","IMPRINT",FACE,{"disambiguationData":[TD([[makeQuery(id+"F16.imprint","IMPRINT",EDGE,{"derivedFrom":sQuery(id+"F16.wireOp",EDGE,"E89.MirrorC")}),1.0]])]});
            var Q1;
            {var subQ1=sQuery(id+"F16.wireOp",EDGE,"E80");Q1=makeQuery(id+"F16.imprint","IMPRINT",FACE,{"disambiguationData":[TD([[makeQuery(id+"F16.imprint","IMPRINT",EDGE,{"derivedFrom":subQ1}),-1.0]])]});}
            var Q2;
            Q2=makeQuery(id+"F16.imprint","IMPRINT",FACE,{"disambiguationData":[TD([[makeQuery(id+"F16.imprint","IMPRINT",EDGE,{"derivedFrom":makeQuery(id+"F1.opExtrude","CAP_EDGE",EDGE,{"disambiguationData":[OSD([sQuery(id+"F0.wireOp",EDGE,"E1.left")])],"isStart":true})}),-1.0]])]});
            var Q3;
            Q3=makeQuery(id+"F2.opExtrude","CAP_FACE",FACE,{"disambiguationData":[OSD([sQuery(id+"F0.wireOp",EDGE,"E12"),sQuery(id+"F0.wireOp",EDGE,"E13"),sQuery(id+"F0.wireOp",EDGE,"E14"),sQuery(id+"F0.wireOp",EDGE,"E15"),sQuery(id+"F0.wireOp",EDGE,"E17.filletArc"),sQuery(id+"F0.wireOp",EDGE,"E18.filletArc"),sQuery(id+"F0.wireOp",EDGE,"E19.filletArc"),sQuery(id+"F0.wireOp",EDGE,"E20.filletArc"),sQuery(id+"F0.wireOp",EDGE,"E25.0"),sQuery(id+"F0.wireOp",EDGE,"E25.1"),sQuery(id+"F0.wireOp",EDGE,"E25.2"),sQuery(id+"F0.wireOp",EDGE,"E25.3"),sQuery(id+"F0.wireOp",EDGE,"E25.4"),sQuery(id+"F0.wireOp",EDGE,"E25.5"),sQuery(id+"F0.wireOp",EDGE,"E25.6"),sQuery(id+"F0.wireOp",EDGE,"E25.7")])],"isStart":false});
            extrude(context, id + "F17", {"entities" : qUnion([Q0, Q1, Q2]), "operationType" : NewBodyOperationType.ADD, "endBound" : BoundingType.UP_TO_SURFACE, "endBoundEntityFace" : qUnion([Q3]), "depth" : 25 * mm});
        }
    });
